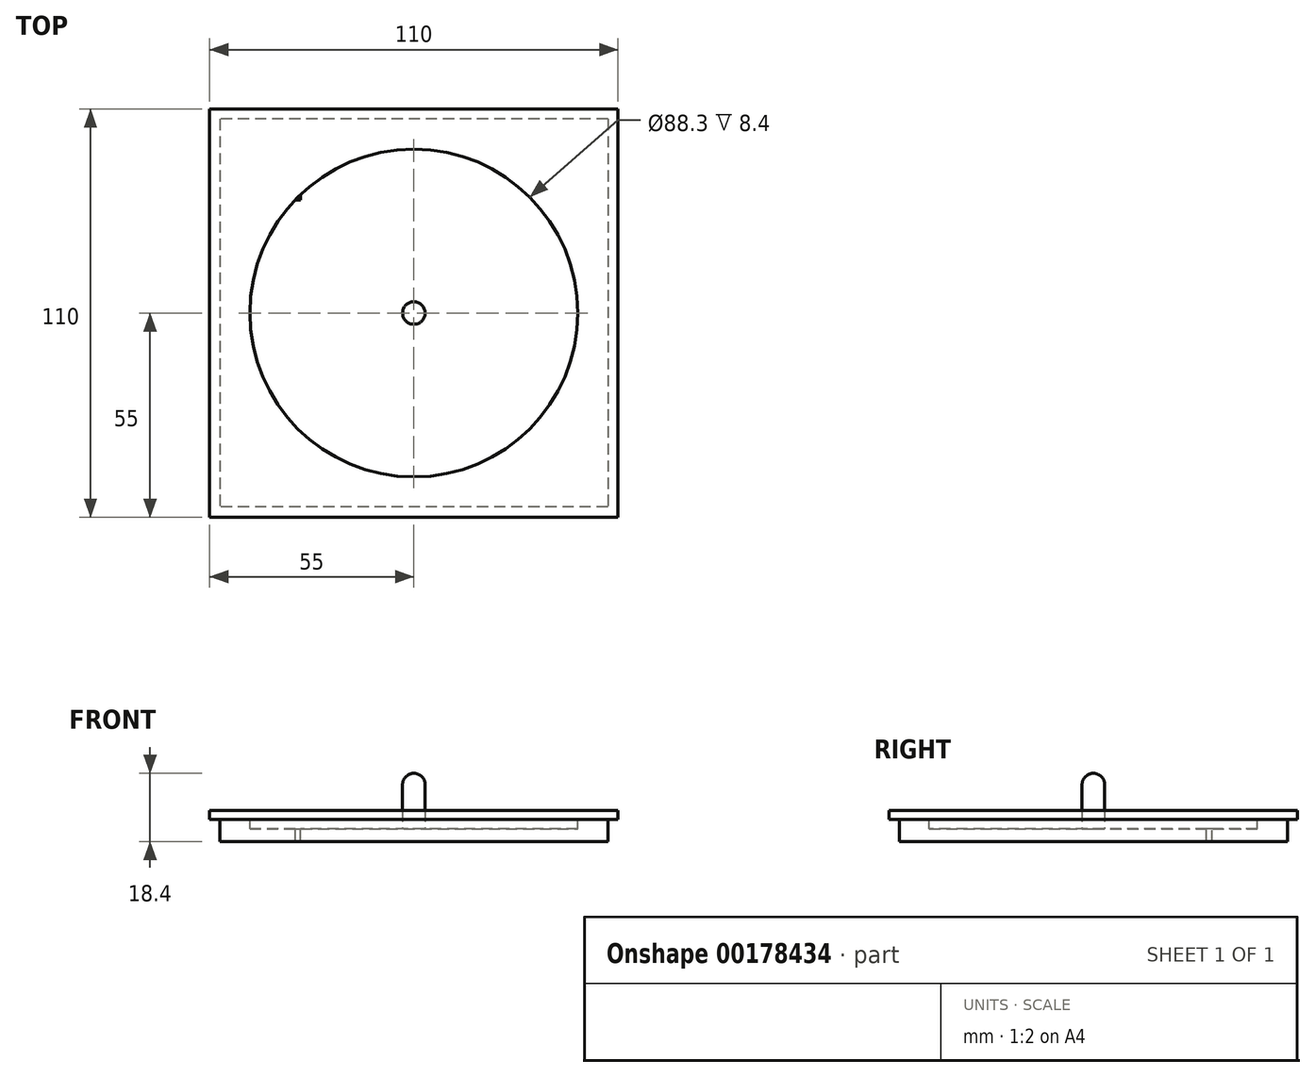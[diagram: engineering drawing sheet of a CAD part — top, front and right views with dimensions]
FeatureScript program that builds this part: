
annotation { "Feature Type Name" : "Feature", "Feature Type Description" : "" }
export const myFeature = defineFeature(function(context is Context, id is Id, definition is map)
    precondition{}
    {
        {
            var Q0;
            Q0=qCreatedBy(makeId("Top.planeOp"),FACE);
            var sketch = newSketch(context, id + "F0", { "sketchPlane" : qUnion([Q0])});
            skLineSegment(sketch, "E0.bottom", {"start": v(52.25, 52.25) * mm, "end": v(-52.25, 52.25) * mm});
            skLineSegment(sketch, "E0.top", {"start": v(52.25, -52.25) * mm, "end": v(-52.25, -52.25) * mm});
            skLineSegment(sketch, "E0.left", {"start": v(52.25, 52.25) * mm, "end": v(52.25, -52.25) * mm});
            skLineSegment(sketch, "E0.right", {"start": v(-52.25, 52.25) * mm, "end": v(-52.25, -52.25) * mm});
            skPoint(sketch, "E0.middle", {"position": v(0, 0) * mm});
            skSolve(sketch);
        }
        {
            var Q0;
            Q0=makeQuery(id+"F0.imprint","IMPRINT",FACE,{"disambiguationData":[TD([[makeQuery(id+"F0.imprint","IMPRINT",EDGE,{"derivedFrom":sQuery(id+"F0.wireOp",EDGE,"E0.bottom")}),1.0]])]});
            extrude(context, id + "F1", {"entities" : qUnion([Q0]), "depth" : 6 * mm});
        }
        {
            var Q0;
            Q0=makeQuery(id+"F1.opExtrude","CAP_FACE",FACE,{"disambiguationData":[OSD([sQuery(id+"F0.wireOp",EDGE,"E0.bottom"),sQuery(id+"F0.wireOp",EDGE,"E0.top"),sQuery(id+"F0.wireOp",EDGE,"E0.left"),sQuery(id+"F0.wireOp",EDGE,"E0.right")])],"isStart":false});
            var sketch = newSketch(context, id + "F2", { "sketchPlane" : qUnion([Q0])});
            skLineSegment(sketch, "E1.bottom", {"start": v(-55, 55) * mm, "end": v(55, 55) * mm});
            skLineSegment(sketch, "E1.top", {"start": v(-55, -55) * mm, "end": v(55, -55) * mm});
            skLineSegment(sketch, "E1.left", {"start": v(-55, 55) * mm, "end": v(-55, -55) * mm});
            skLineSegment(sketch, "E1.right", {"start": v(55, 55) * mm, "end": v(55, -55) * mm});
            skPoint(sketch, "E1.middle", {"position": v(0, 0) * mm});
            skSolve(sketch);
        }
        {
            var Q0;
            Q0=makeQuery(id+"F2.imprint","IMPRINT",FACE,{"disambiguationData":[TD([[makeQuery(id+"F2.imprint","IMPRINT",EDGE,{"derivedFrom":sQuery(id+"F2.wireOp",EDGE,"E1.bottom")}),-1.0]])]});
            var Q1;
            Q1=makeQuery(id+"F2.imprint","IMPRINT",FACE,{"disambiguationData":[TD([[makeQuery(id+"F2.imprint","IMPRINT",EDGE,{"derivedFrom":makeQuery(id+"F1.opExtrude","CAP_EDGE",EDGE,{"disambiguationData":[OSD([sQuery(id+"F0.wireOp",EDGE,"E0.bottom")])],"isStart":false})}),1.0]])]});
            extrude(context, id + "F3", {"entities" : qUnion([Q0, Q1]), "operationType" : NewBodyOperationType.ADD, "depth" : 2.4 * mm});
        }
        {
            var Q0;
            Q0=makeQuery(id+"F3.opExtrude","CAP_FACE",FACE,{"disambiguationData":[OSD([sQuery(id+"F2.wireOp",EDGE,"E1.bottom"),sQuery(id+"F2.wireOp",EDGE,"E1.top"),sQuery(id+"F2.wireOp",EDGE,"E1.left"),sQuery(id+"F2.wireOp",EDGE,"E1.right")])],"isStart":false});
            var sketch = newSketch(context, id + "F4", { "sketchPlane" : qUnion([Q0])});
            skCircle(sketch, "E2", {"center": v(0, 0) * mm, "radius": 3.03 * mm});
            skSolve(sketch);
        }
        {
            var Q0;
            Q0=makeQuery(id+"F4.imprint","IMPRINT",FACE,{"disambiguationData":[TD([[makeQuery(id+"F4.imprint","IMPRINT",EDGE,{"derivedFrom":sQuery(id+"F4.wireOp",EDGE,"E2")}),1.0]])]});
            extrude(context, id + "F5", {"entities" : qUnion([Q0]), "operationType" : NewBodyOperationType.ADD, "depth" : 10 * mm});
        }
        {
            var Q0;
            Q0=makeQuery(id+"F3.opExtrude","CAP_FACE",FACE,{"disambiguationData":[OSD([sQuery(id+"F2.wireOp",EDGE,"E1.bottom"),sQuery(id+"F2.wireOp",EDGE,"E1.top"),sQuery(id+"F2.wireOp",EDGE,"E1.left"),sQuery(id+"F2.wireOp",EDGE,"E1.right")])],"isStart":false});
            var sketch = newSketch(context, id + "F6", { "sketchPlane" : qUnion([Q0])});
            skCircle(sketch, "E3", {"center": v(0, 0) * mm, "radius": 44.15 * mm});
            skSolve(sketch);
        }
        {
            var Q0;
            Q0=makeQuery(id+"F6.imprint","IMPRINT",FACE,{"disambiguationData":[TD([[makeQuery(id+"F6.imprint","IMPRINT",EDGE,{"derivedFrom":sQuery(id+"F6.wireOp",EDGE,"E3")}),1.0]])]});
            extrude(context, id + "F7", {"entities" : qUnion([Q0]), "operationType" : NewBodyOperationType.REMOVE, "oppositeDirection" : true, "depth" : 5 * mm});
        }
        {
            var Q0;
            Q0=makeQuery(id+"F5.opExtrude","CAP_EDGE",EDGE,{"disambiguationData":[OSD([sQuery(id+"F4.wireOp",EDGE,"E2")])],"isStart":false});
            fillet(context, id + "F8", {"entities" : qUnion([Q0]), "radius" : 3 * mm, "tangentPropagation" : true, "allowEdgeOverflow" : false});
        }
        {
            var Q0;
            Q0=makeQuery(id+"F3.opExtrude","CAP_FACE",FACE,{"disambiguationData":[OSD([sQuery(id+"F2.wireOp",EDGE,"E1.bottom"),sQuery(id+"F2.wireOp",EDGE,"E1.top"),sQuery(id+"F2.wireOp",EDGE,"E1.left"),sQuery(id+"F2.wireOp",EDGE,"E1.right")])],"isStart":false});
            var sketch = newSketch(context, id + "F9", { "sketchPlane" : qUnion([Q0])});
            skLineSegment(sketch, "E4.0.0", {"start": v(55, 55) * mm, "end": v(-55, 55) * mm});
            skLineSegment(sketch, "E4.0.1", {"start": v(-55, 55) * mm, "end": v(-55, -55) * mm});
            skLineSegment(sketch, "E4.0.2", {"start": v(-55, -55) * mm, "end": v(55, -55) * mm});
            skLineSegment(sketch, "E4.0.3", {"start": v(55, -55) * mm, "end": v(55, 55) * mm});
            skLineSegment(sketch, "E5.bottom", {"start": v(-55, 55) * mm, "end": v(-30.5, 55) * mm});
            skLineSegment(sketch, "E5.top", {"start": v(-55, 30.5) * mm, "end": v(-30.5, 30.5) * mm});
            skLineSegment(sketch, "E5.left", {"start": v(-55, 55) * mm, "end": v(-55, 30.5) * mm});
            skLineSegment(sketch, "E5.right", {"start": v(-30.5, 55) * mm, "end": v(-30.5, 30.5) * mm});
            skSolve(sketch);
        }
        {
            var Q0;
            {var subQ1=sQuery(id+"F9.wireOp",EDGE,"E5.bottom");Q0=makeQuery(id+"F9.imprint","IMPRINT",FACE,{"disambiguationData":[TD([[makeQuery(id+"F9.imprint","IMPRINT",EDGE,{"derivedFrom":subQ1}),-1.0]])]});}
            var Q1;
            {var subQ0=sQuery(id+"F9.wireOp",EDGE,"E5.right");var subQ1=sQuery(id+"F9.wireOp",EDGE,"E5.top");var subQ2=makeQuery(id+"F9.imprint","INTERSECT",VERTEX,{"derivedFrom":[subQ1,subQ0]});Q1=makeQuery(id+"F9.imprint","IMPRINT",FACE,{"disambiguationData":[TD([[makeQuery(id+"F9.imprint","IMPRINT",EDGE,{"disambiguationData":[TD([[subQ2,1.0]])],"derivedFrom":subQ1}),1.0]])]});}
            extrude(context, id + "F10", {"entities" : qUnion([Q0, Q1]), "operationType" : NewBodyOperationType.REMOVE, "endBound" : BoundingType.THROUGH_ALL, "oppositeDirection" : true, "depth" : 25 * mm});
        }
        {
            var Q0;
            Q0=qCreatedBy(makeId("Right.planeOp"),FACE);
            var sketch = newSketch(context, id + "F11", { "sketchPlane" : qUnion([Q0])});
            skLineSegment(sketch, "E6", {"start": v(0, 0) * mm, "end": v(0, 53.32) * mm});
            skSolve(sketch);
        }
    });
